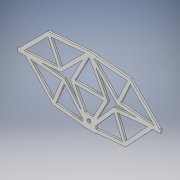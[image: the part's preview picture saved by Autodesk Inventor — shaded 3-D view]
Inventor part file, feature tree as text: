
AUTODESK INVENTOR PART (.ipt)
format: ipt  version: 2018 (Build 220112000, 112)  size: 237,568 bytes
history: native  units: in
note: dims shown in document units (in); Inventor stores cm internally (conversion verified against a paired STEP export)
features: extrude x1, sketch x1
ambient origin geometry x8: Origin, YZ Plane, XZ Plane, XY Plane, X Axis, Y Axis, Z Axis, Center Point
bodies: Solid1 (feature_tree)
feature tree (2):
  extrude  "Extrusion1"  Depth=0.125in
  sketch  "Sketch1"  dims[d1=10.5in d2=5.0in d4=45.0deg d6=0.0327in d7=1.2041in d9=0.0327in d10=2.5in d11=5.25in d12=0.125in d13=135.0deg d14=0.125in d16=135.0deg d17=0.125in d18=2.5in d19=1.2041in d20=45.0deg d21=45.0deg d22=1.25in d23=1.25in d24=2.375in d25=5.25in d26=0.125in d27=0.9045in d29=1.2012in d30=2.625in d31=1.875in d32=0.5in d33=4.75in d34=1.0in d37=0.5583in d38=0.2791in d45=0.25in d46=0.125in d47=0.125in d48=0.125in d49=0.125in d50=0.125in d51=0.125in d53=0.25in d54=0.25in d55=0.25in d56=0.25in d57=0.125in d58=0.25in d59=0.25in d60=0.125in d61=0.125in d62=0.25in d63=0.125in d67=0.25in d68=0.125in d69=0.25in d70=0.25in d71=0.25in d72=0.125in d73=0.125in d74=0.25in d75=0.25in d76=0.125in d77=1.043in d78=0.25in d80=0.125in d81=0.0in]
